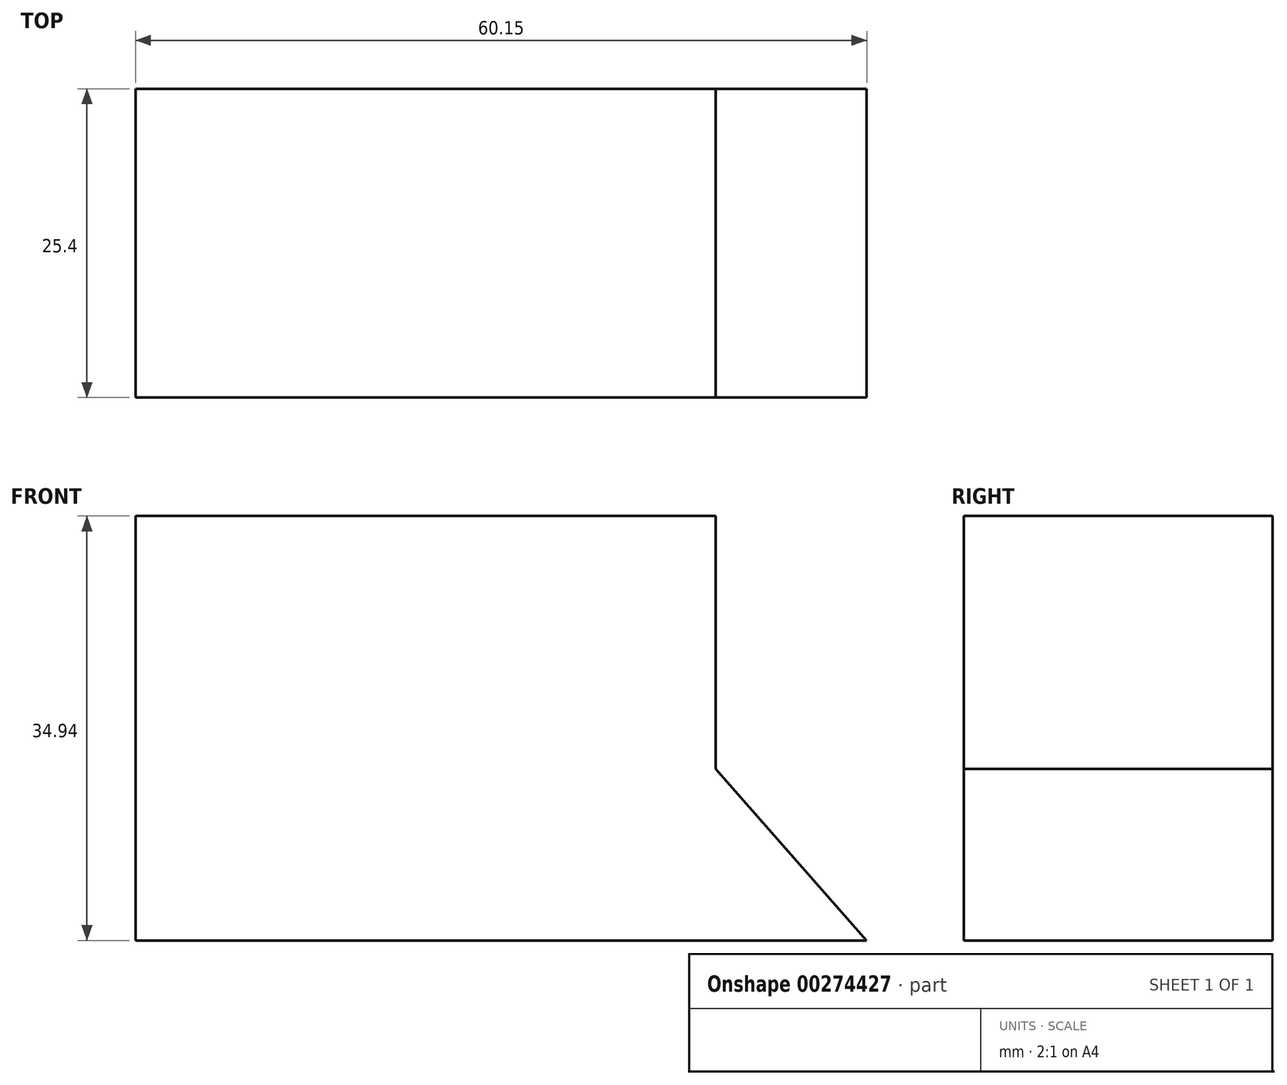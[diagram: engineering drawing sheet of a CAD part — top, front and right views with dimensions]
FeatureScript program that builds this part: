
annotation { "Feature Type Name" : "Feature", "Feature Type Description" : "" }
export const myFeature = defineFeature(function(context is Context, id is Id, definition is map)
    precondition{}
    {
        {
            var Q0;
            Q0=qCreatedBy(makeId("Front.planeOp"),FACE);
            var sketch = newSketch(context, id + "F0", { "sketchPlane" : qUnion([Q0])});
            skLineSegment(sketch, "E0.bottom", {"start": v(-62.82, 38.2) * mm, "end": v(-15.09, 38.2) * mm});
            skLineSegment(sketch, "E0.top", {"start": v(-62.82, 3.25) * mm, "end": v(-15.09, 3.25) * mm});
            skLineSegment(sketch, "E0.left", {"start": v(-62.82, 38.2) * mm, "end": v(-62.82, 3.25) * mm});
            skLineSegment(sketch, "E0.right", {"start": v(-15.09, 38.2) * mm, "end": v(-15.09, 3.25) * mm});
            skLineSegment(sketch, "E1", {"start": v(-15.09, 17.38) * mm, "end": v(-2.67, 3.25) * mm});
            skLineSegment(sketch, "E2", {"start": v(-2.67, 3.25) * mm, "end": v(-15.09, 3.25) * mm});
            skSolve(sketch);
        }
        {
            var Q0;
            Q0 = qSketchRegion(id + "F0", true);
            extrude(context, id + "F1", {"entities" : qUnion([Q0]), "depth" : 25.4 * mm});
        }
    });
